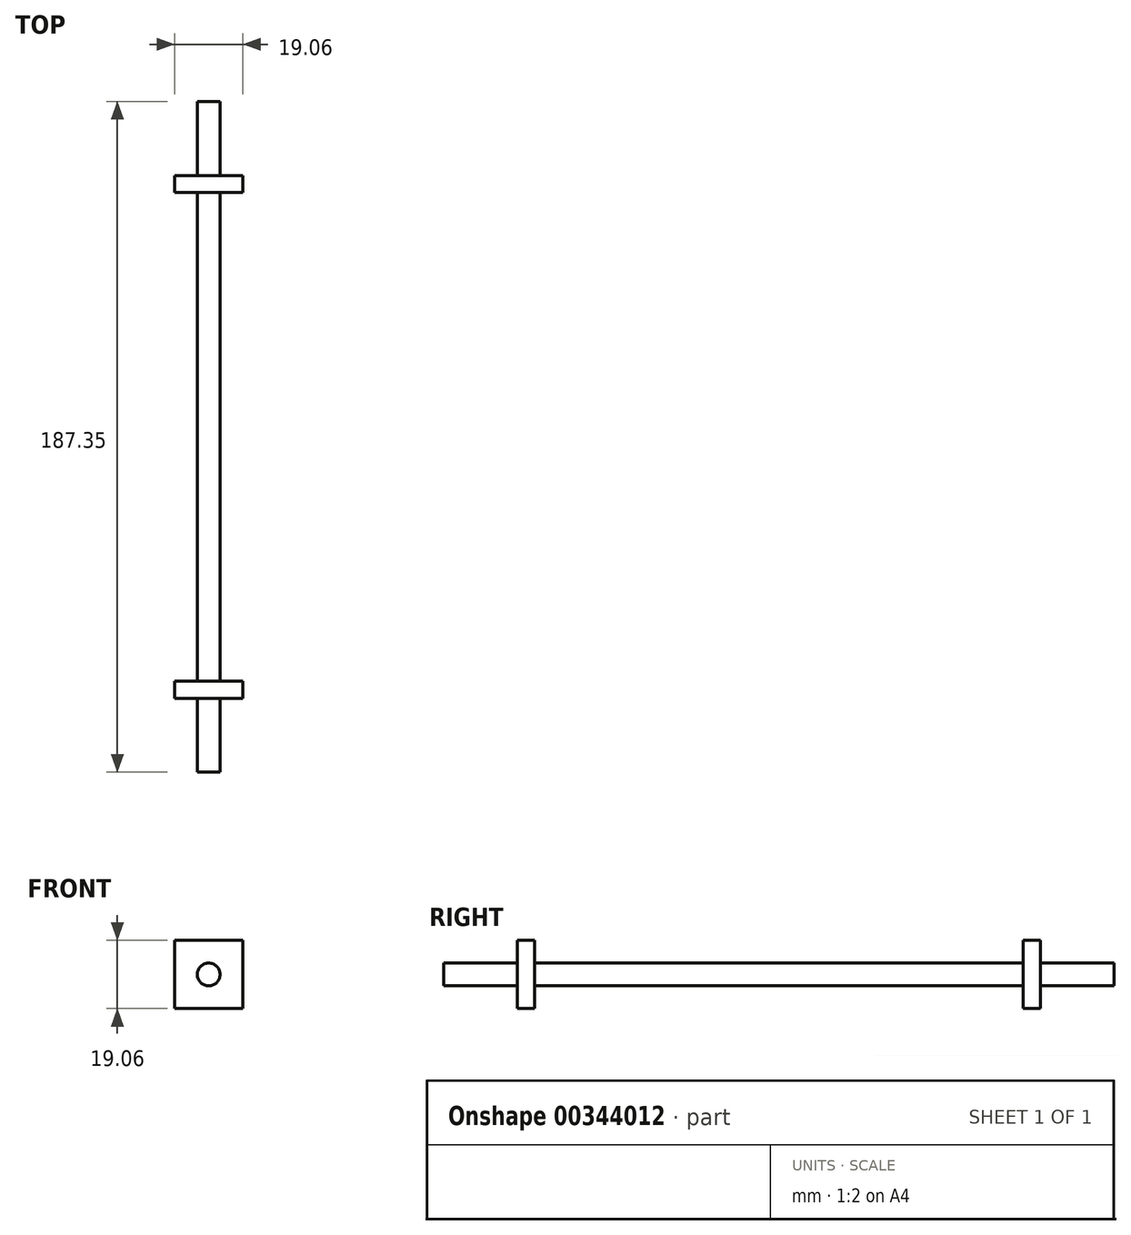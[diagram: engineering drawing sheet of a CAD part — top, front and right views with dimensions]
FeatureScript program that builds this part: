
annotation { "Feature Type Name" : "Feature", "Feature Type Description" : "" }
export const myFeature = defineFeature(function(context is Context, id is Id, definition is map)
    precondition{}
    {
        {
            var Q0;
            Q0=qCreatedBy(makeId("Front.planeOp"),FACE);
            var sketch = newSketch(context, id + "F0", { "sketchPlane" : qUnion([Q0])});
            skCircle(sketch, "E0", {"center": v(0, 0) * mm, "radius": 3.18 * mm});
            skSolve(sketch);
        }
        {
            var Q0;
            Q0 = qSketchRegion(id + "F0", true);
            extrude(context, id + "F1", {"entities" : qUnion([Q0]), "depth" : 136.55 * mm});
        }
        {
            var Q0;
            Q0=makeQuery(id+"F1.opExtrude","CAP_FACE",FACE,{"disambiguationData":[OSD([sQuery(id+"F0.wireOp",EDGE,"E0")])],"isStart":false});
            var sketch = newSketch(context, id + "F2", { "sketchPlane" : qUnion([Q0])});
            skLineSegment(sketch, "E1.bottom", {"start": v(-9.53, 9.53) * mm, "end": v(9.53, 9.53) * mm});
            skLineSegment(sketch, "E1.top", {"start": v(-9.53, -9.53) * mm, "end": v(9.53, -9.53) * mm});
            skLineSegment(sketch, "E1.left", {"start": v(-9.53, 9.53) * mm, "end": v(-9.53, -9.53) * mm});
            skLineSegment(sketch, "E1.right", {"start": v(9.53, 9.53) * mm, "end": v(9.53, -9.53) * mm});
            skSolve(sketch);
        }
        {
            var Q0;
            Q0 = qSketchRegion(id + "F2", true);
            extrude(context, id + "F3", {"entities" : qUnion([Q0]), "operationType" : NewBodyOperationType.ADD, "depth" : 4.76 * mm});
        }
        {
            var Q0;
            Q0=makeQuery(id+"F1.opExtrude","CAP_FACE",FACE,{"disambiguationData":[OSD([sQuery(id+"F0.wireOp",EDGE,"E0")])],"isStart":true});
            var sketch = newSketch(context, id + "F4", { "sketchPlane" : qUnion([Q0])});
            skLineSegment(sketch, "E2.bottom", {"start": v(-9.53, 9.53) * mm, "end": v(9.53, 9.53) * mm});
            skLineSegment(sketch, "E2.top", {"start": v(-9.53, -9.52) * mm, "end": v(9.53, -9.52) * mm});
            skLineSegment(sketch, "E2.left", {"start": v(-9.53, 9.53) * mm, "end": v(-9.53, -9.53) * mm});
            skLineSegment(sketch, "E2.right", {"start": v(9.53, 9.53) * mm, "end": v(9.53, -9.53) * mm});
            skSolve(sketch);
        }
        {
            var Q0;
            Q0 = qSketchRegion(id + "F4", true);
            extrude(context, id + "F5", {"entities" : qUnion([Q0]), "operationType" : NewBodyOperationType.ADD, "depth" : 4.76 * mm});
        }
        {
            var Q0;
            Q0=makeQuery(id+"F2.imprint","IMPRINT",FACE,{"disambiguationData":[TD([[makeQuery(id+"F2.imprint","IMPRINT",EDGE,{"derivedFrom":makeQuery(id+"F1.opExtrude","CAP_EDGE",EDGE,{"disambiguationData":[OSD([sQuery(id+"F0.wireOp",EDGE,"E0")])],"isStart":false})}),1.0]])]});
            var sketch = newSketch(context, id + "F6", { "sketchPlane" : qUnion([Q0])});
            skCircle(sketch, "E3", {"center": v(0, 0) * mm, "radius": 3.18 * mm});
            skSolve(sketch);
        }
        {
            var Q0;
            Q0 = qSketchRegion(id + "F6", true);
            extrude(context, id + "F7", {"entities" : qUnion([Q0]), "operationType" : NewBodyOperationType.ADD, "depth" : 25.4 * mm});
        }
        {
            var Q0;
            Q0=makeQuery(id+"F4.imprint","IMPRINT",FACE,{"disambiguationData":[TD([[makeQuery(id+"F4.imprint","IMPRINT",EDGE,{"derivedFrom":makeQuery(id+"F1.opExtrude","CAP_EDGE",EDGE,{"disambiguationData":[OSD([sQuery(id+"F0.wireOp",EDGE,"E0")])],"isStart":true})}),-1.0]])]});
            var sketch = newSketch(context, id + "F8", { "sketchPlane" : qUnion([Q0])});
            skCircle(sketch, "E4", {"center": v(0, 0) * mm, "radius": 3.18 * mm});
            skSolve(sketch);
        }
        {
            var Q0;
            Q0 = qSketchRegion(id + "F8", true);
            extrude(context, id + "F9", {"entities" : qUnion([Q0]), "operationType" : NewBodyOperationType.ADD, "depth" : 25.4 * mm});
        }
    });
